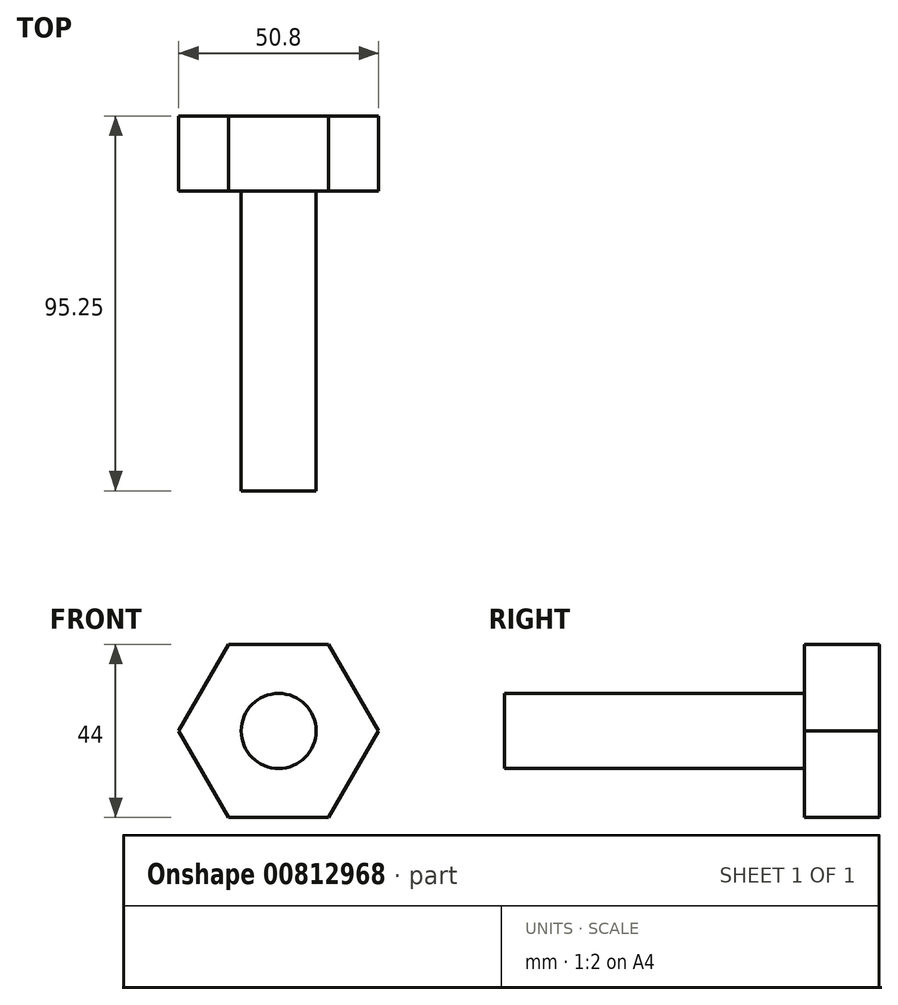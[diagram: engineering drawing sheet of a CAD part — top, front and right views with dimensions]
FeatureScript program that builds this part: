
annotation { "Feature Type Name" : "Feature", "Feature Type Description" : "" }
export const myFeature = defineFeature(function(context is Context, id is Id, definition is map)
    precondition{}
    {
        {
            var Q0;
            Q0=qCreatedBy(makeId("Front.planeOp"),FACE);
            var sketch = newSketch(context, id + "F0", { "sketchPlane" : qUnion([Q0])});
            skCircle(sketch, "E0.cCircle", {"center": v(0, 0) * mm, "radius": 25.4 * mm, "construction": true});
            skLineSegment(sketch, "E0.0", {"start": v(25.4, 0) * mm, "end": v(12.7, -22) * mm});
            skLineSegment(sketch, "E0.1", {"start": v(12.7, -22) * mm, "end": v(-12.7, -22) * mm});
            skLineSegment(sketch, "E0.2", {"start": v(-12.7, -22) * mm, "end": v(-25.4, 0) * mm});
            skLineSegment(sketch, "E0.3", {"start": v(-25.4, 0) * mm, "end": v(-12.7, 22) * mm});
            skLineSegment(sketch, "E0.4", {"start": v(-12.7, 22) * mm, "end": v(12.7, 22) * mm});
            skLineSegment(sketch, "E0.5", {"start": v(12.7, 22) * mm, "end": v(25.4, 0) * mm});
            skSolve(sketch);
        }
        {
            var Q0;
            Q0 = qSketchRegion(id + "F0", true);
            extrude(context, id + "F1", {"entities" : qUnion([Q0]), "depth" : 19.05 * mm, "offsetDistance" : 25.4 * mm});
        }
        {
            var Q0;
            Q0=makeQuery(id+"F1.opExtrude","CAP_FACE",FACE,{"disambiguationData":[OSD([sQuery(id+"F0.wireOp",EDGE,"E0.0"),sQuery(id+"F0.wireOp",EDGE,"E0.1"),sQuery(id+"F0.wireOp",EDGE,"E0.2"),sQuery(id+"F0.wireOp",EDGE,"E0.3"),sQuery(id+"F0.wireOp",EDGE,"E0.4"),sQuery(id+"F0.wireOp",EDGE,"E0.5")])],"isStart":false});
            var sketch = newSketch(context, id + "F2", { "sketchPlane" : qUnion([Q0])});
            skCircle(sketch, "E1", {"center": v(0, 0) * mm, "radius": 9.53 * mm});
            skSolve(sketch);
        }
        {
            var Q0;
            Q0 = qSketchRegion(id + "F2", true);
            extrude(context, id + "F3", {"entities" : qUnion([Q0]), "operationType" : NewBodyOperationType.ADD, "depth" : 76.2 * mm, "offsetDistance" : 25.4 * mm});
        }
    });
